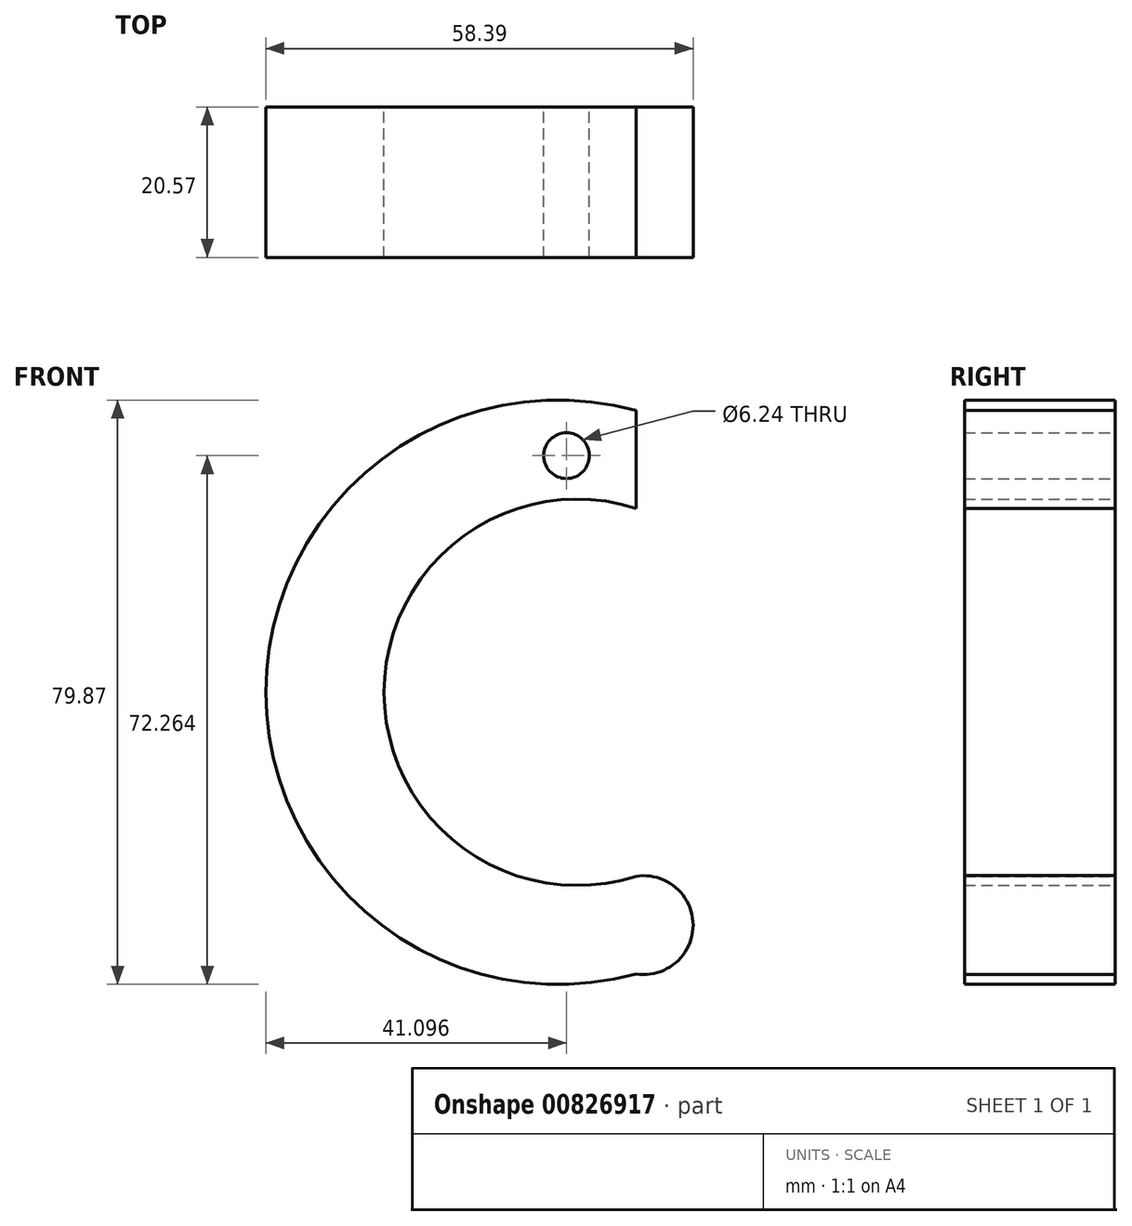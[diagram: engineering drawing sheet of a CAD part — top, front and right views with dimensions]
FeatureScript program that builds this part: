
annotation { "Feature Type Name" : "Feature", "Feature Type Description" : "" }
export const myFeature = defineFeature(function(context is Context, id is Id, definition is map)
    precondition{}
    {
        {
            var Q0;
            Q0=qCreatedBy(makeId("Front.planeOp"),FACE);
            var sketch = newSketch(context, id + "F0", { "sketchPlane" : qUnion([Q0])});
            skArc(sketch, "E0", {"start": v(0, 42.08) * mm, "mid": v(-50.59, 3.6) * mm, "end": v(0, -34.9) * mm});
            skArc(sketch, "E1", {"start": v(0, 28.74) * mm, "mid": v(-34.43, 3.59) * mm, "end": v(0, -21.56) * mm});
            skLineSegment(sketch, "E2", {"start": v(0, 42.08) * mm, "end": v(0, 28.74) * mm});
            skArc(sketch, "E3", {"start": v(0, -34.9) * mm, "mid": v(7.8, -28.23) * mm, "end": v(0, -21.56) * mm});
            skCircle(sketch, "E4", {"center": v(-9.5, 35.92) * mm, "radius": 3.12 * mm});
            skSolve(sketch);
        }
        {
            var Q0;
            Q0 = qSketchRegion(id + "F0", true);
            extrude(context, id + "F1", {"entities" : qUnion([Q0]), "depth" : 20.57 * mm, "offsetDistance" : 25.4 * mm});
        }
    });
